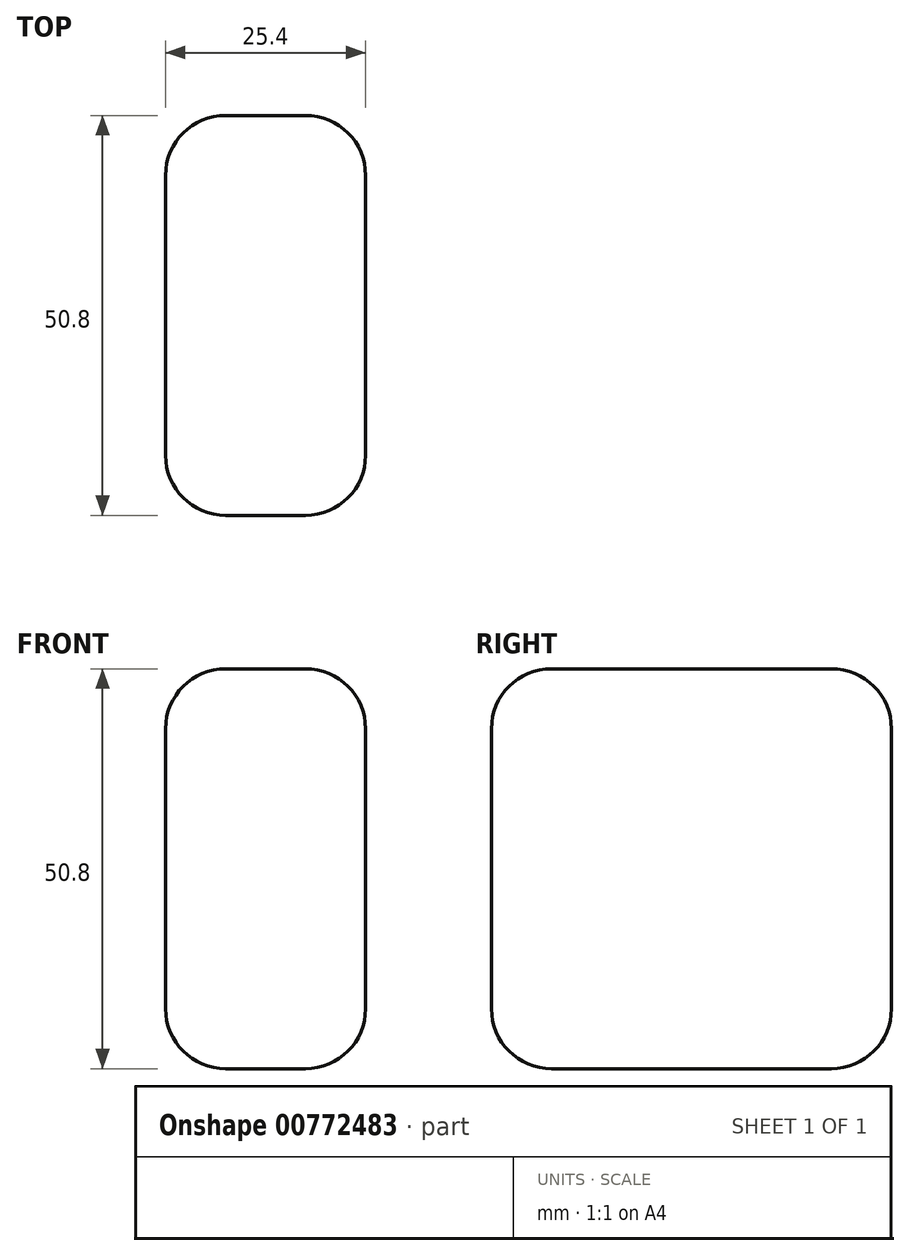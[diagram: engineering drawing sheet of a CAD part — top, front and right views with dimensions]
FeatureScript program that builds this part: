
annotation { "Feature Type Name" : "Feature", "Feature Type Description" : "" }
export const myFeature = defineFeature(function(context is Context, id is Id, definition is map)
    precondition{}
    {
        {
            var Q0;
            Q0=qCreatedBy(makeId("Top.planeOp"),FACE);
            var sketch = newSketch(context, id + "F0", { "sketchPlane" : qUnion([Q0])});
            skLineSegment(sketch, "E0.bottom", {"start": v(-18.88, 25.4) * mm, "end": v(6.52, 25.4) * mm});
            skLineSegment(sketch, "E0.top", {"start": v(-18.88, -25.4) * mm, "end": v(6.52, -25.4) * mm});
            skLineSegment(sketch, "E0.left", {"start": v(-18.88, 25.4) * mm, "end": v(-18.88, -25.4) * mm});
            skLineSegment(sketch, "E0.right", {"start": v(6.52, 25.4) * mm, "end": v(6.52, -25.4) * mm});
            skPoint(sketch, "E0.middle", {"position": v(-6.18, 0) * mm});
            skSolve(sketch);
        }
        {
            var Q0;
            Q0=makeQuery(id+"F0.imprint","IMPRINT",FACE,{"disambiguationData":[TD([[makeQuery(id+"F0.imprint","IMPRINT",EDGE,{"derivedFrom":sQuery(id+"F0.wireOp",EDGE,"E0.bottom")}),-1.0]])]});
            extrude(context, id + "F1", {"entities" : qUnion([Q0]), "depth" : 50.8 * mm, "offsetDistance" : 25.4 * mm});
        }
        {
            var Q0;
            Q0=makeQuery(id+"F1.opExtrude","CAP_EDGE",EDGE,{"disambiguationData":[OSD([sQuery(id+"F0.wireOp",EDGE,"E0.left")])],"isStart":false});
            var Q1;
            Q1=makeQuery(id+"F1.opExtrude","CAP_EDGE",EDGE,{"disambiguationData":[OSD([sQuery(id+"F0.wireOp",EDGE,"E0.top")])],"isStart":false});
            var Q2;
            Q2=makeQuery(id+"F1.opExtrude","CAP_EDGE",EDGE,{"disambiguationData":[OSD([sQuery(id+"F0.wireOp",EDGE,"E0.right")])],"isStart":false});
            var Q3;
            Q3=makeQuery(id+"F1.opExtrude","SWEPT_EDGE",EDGE,{"disambiguationData":[OSD([sQuery(id+"F0.wireOp",EDGE,"E0.top"),sQuery(id+"F0.wireOp",EDGE,"E0.right")])]});
            var Q4;
            Q4=makeQuery(id+"F1.opExtrude","SWEPT_EDGE",EDGE,{"disambiguationData":[OSD([sQuery(id+"F0.wireOp",EDGE,"E0.top"),sQuery(id+"F0.wireOp",EDGE,"E0.left")])]});
            var Q5;
            Q5=makeQuery(id+"F1.opExtrude","CAP_EDGE",EDGE,{"disambiguationData":[OSD([sQuery(id+"F0.wireOp",EDGE,"E0.top")])],"isStart":true});
            var Q6;
            Q6=makeQuery(id+"F1.opExtrude","CAP_EDGE",EDGE,{"disambiguationData":[OSD([sQuery(id+"F0.wireOp",EDGE,"E0.left")])],"isStart":true});
            var Q7;
            Q7=makeQuery(id+"F1.opExtrude","CAP_EDGE",EDGE,{"disambiguationData":[OSD([sQuery(id+"F0.wireOp",EDGE,"E0.right")])],"isStart":true});
            var Q8;
            Q8=makeQuery(id+"F1.opExtrude","SWEPT_EDGE",EDGE,{"disambiguationData":[OSD([sQuery(id+"F0.wireOp",EDGE,"E0.bottom"),sQuery(id+"F0.wireOp",EDGE,"E0.right")])]});
            var Q9;
            Q9=makeQuery(id+"F1.opExtrude","SWEPT_EDGE",EDGE,{"disambiguationData":[OSD([sQuery(id+"F0.wireOp",EDGE,"E0.bottom"),sQuery(id+"F0.wireOp",EDGE,"E0.left")])]});
            var Q10;
            Q10=makeQuery(id+"F1.opExtrude","CAP_EDGE",EDGE,{"disambiguationData":[OSD([sQuery(id+"F0.wireOp",EDGE,"E0.bottom")])],"isStart":false});
            var Q11;
            Q11=makeQuery(id+"F1.opExtrude","CAP_EDGE",EDGE,{"disambiguationData":[OSD([sQuery(id+"F0.wireOp",EDGE,"E0.bottom")])],"isStart":true});
            fillet(context, id + "F2", {"entities" : qUnion([Q0, Q1, Q2, Q3, Q4, Q5, Q6, Q7, Q8, Q9, Q10, Q11]), "radius" : 7.62 * mm, "tangentPropagation" : true, "defaultsChanged" : false, "vertexSettings" : [], "allowEdgeOverflow" : false});
        }
    });
